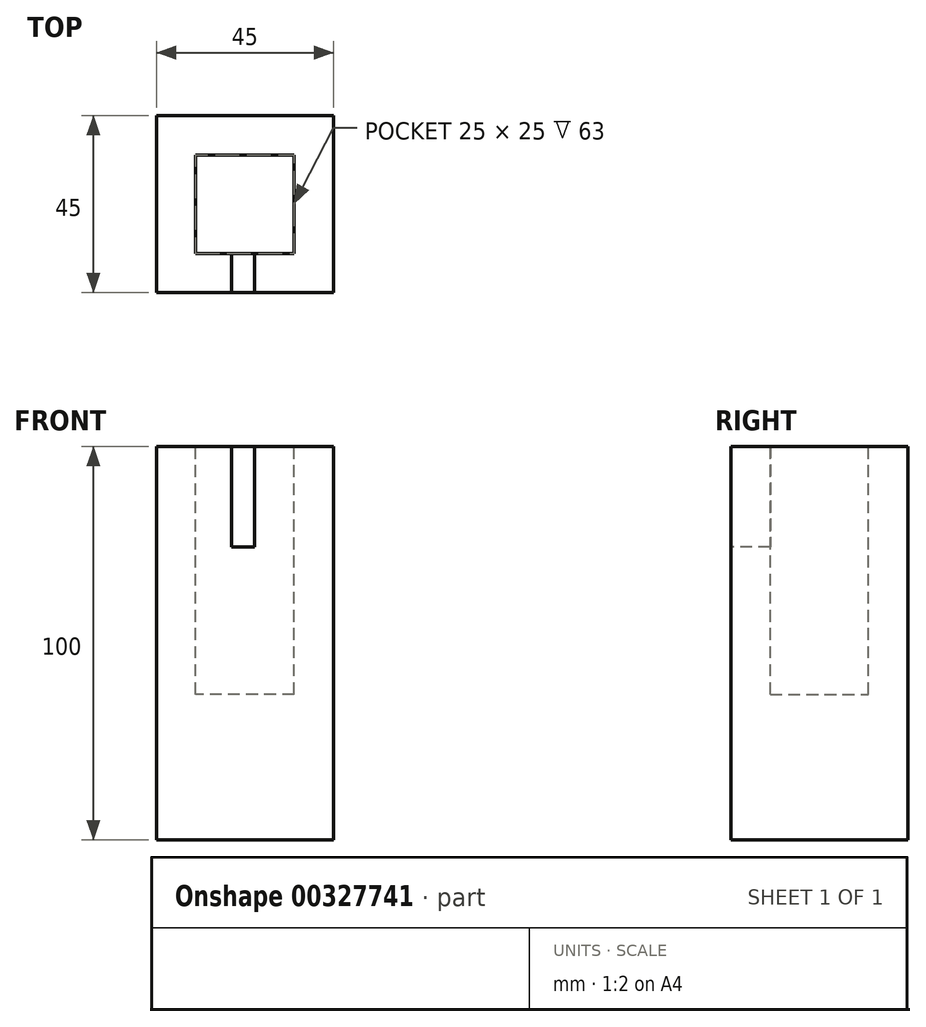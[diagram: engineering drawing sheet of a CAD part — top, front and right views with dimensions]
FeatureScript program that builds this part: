
annotation { "Feature Type Name" : "Feature", "Feature Type Description" : "" }
export const myFeature = defineFeature(function(context is Context, id is Id, definition is map)
    precondition{}
    {
        {
            var Q0;
            Q0=qCreatedBy(makeId("Top.planeOp"),FACE);
            var sketch = newSketch(context, id + "F0", { "sketchPlane" : qUnion([Q0])});
            skLineSegment(sketch, "E0.bottom", {"start": v(22.5, -22.5) * mm, "end": v(-22.5, -22.5) * mm});
            skLineSegment(sketch, "E0.top", {"start": v(22.5, 22.5) * mm, "end": v(-22.5, 22.5) * mm});
            skLineSegment(sketch, "E0.left", {"start": v(22.5, -22.5) * mm, "end": v(22.5, 22.5) * mm});
            skLineSegment(sketch, "E0.right", {"start": v(-22.5, -22.5) * mm, "end": v(-22.5, 22.5) * mm});
            skPoint(sketch, "E0.middle", {"position": v(0, 0) * mm});
            skSolve(sketch);
        }
        {
            var Q0;
            Q0=makeQuery(id+"F0.imprint","IMPRINT",FACE,{"disambiguationData":[TD([[makeQuery(id+"F0.imprint","IMPRINT",EDGE,{"derivedFrom":sQuery(id+"F0.wireOp",EDGE,"E0.bottom")}),-1.0]])]});
            extrude(context, id + "F1", {"entities" : qUnion([Q0]), "depth" : 100 * mm});
        }
        {
            var Q0;
            Q0=makeQuery(id+"F1.opExtrude","CAP_FACE",FACE,{"disambiguationData":[OSD([sQuery(id+"F0.wireOp",EDGE,"E0.bottom"),sQuery(id+"F0.wireOp",EDGE,"E0.top"),sQuery(id+"F0.wireOp",EDGE,"E0.left"),sQuery(id+"F0.wireOp",EDGE,"E0.right")])],"isStart":false});
            var sketch = newSketch(context, id + "F2", { "sketchPlane" : qUnion([Q0])});
            skLineSegment(sketch, "E1.bottom", {"start": v(12.5, -12.5) * mm, "end": v(-12.5, -12.5) * mm});
            skLineSegment(sketch, "E1.top", {"start": v(12.5, 12.5) * mm, "end": v(-12.5, 12.5) * mm});
            skLineSegment(sketch, "E1.left", {"start": v(12.5, -12.5) * mm, "end": v(12.5, 12.5) * mm});
            skLineSegment(sketch, "E1.right", {"start": v(-12.5, -12.5) * mm, "end": v(-12.5, 12.5) * mm});
            skPoint(sketch, "E1.middle", {"position": v(0, 0) * mm});
            skSolve(sketch);
        }
        {
            var Q0;
            Q0=makeQuery(id+"F2.imprint","IMPRINT",FACE,{"disambiguationData":[TD([[makeQuery(id+"F2.imprint","IMPRINT",EDGE,{"derivedFrom":sQuery(id+"F2.wireOp",EDGE,"E1.bottom")}),-1.0]])]});
            extrude(context, id + "F3", {"entities" : qUnion([Q0]), "operationType" : NewBodyOperationType.REMOVE, "oppositeDirection" : true, "depth" : 63 * mm});
        }
        {
            var Q0;
            Q0=makeQuery(id+"F1.opExtrude","SWEPT_FACE",FACE,{"disambiguationData":[OSD([sQuery(id+"F0.wireOp",EDGE,"E0.bottom")])]});
            var sketch = newSketch(context, id + "F4", { "sketchPlane" : qUnion([Q0])});
            skLineSegment(sketch, "E2.bottom", {"start": v(-3.38, 100) * mm, "end": v(2.47, 100) * mm});
            skLineSegment(sketch, "E2.top", {"start": v(-3.38, 74.46) * mm, "end": v(2.47, 74.46) * mm});
            skLineSegment(sketch, "E2.left", {"start": v(-3.38, 100) * mm, "end": v(-3.38, 74.46) * mm});
            skLineSegment(sketch, "E2.right", {"start": v(2.47, 100) * mm, "end": v(2.47, 74.46) * mm});
            skSolve(sketch);
        }
        {
            var Q0;
            Q0=makeQuery(id+"F4.imprint","IMPRINT",FACE,{"disambiguationData":[TD([[makeQuery(id+"F4.imprint","IMPRINT",EDGE,{"derivedFrom":sQuery(id+"F4.wireOp",EDGE,"E2.bottom")}),1.0]])]});
            extrude(context, id + "F5", {"entities" : qUnion([Q0]), "operationType" : NewBodyOperationType.REMOVE, "oppositeDirection" : true, "depth" : 10 * mm});
        }
    });
